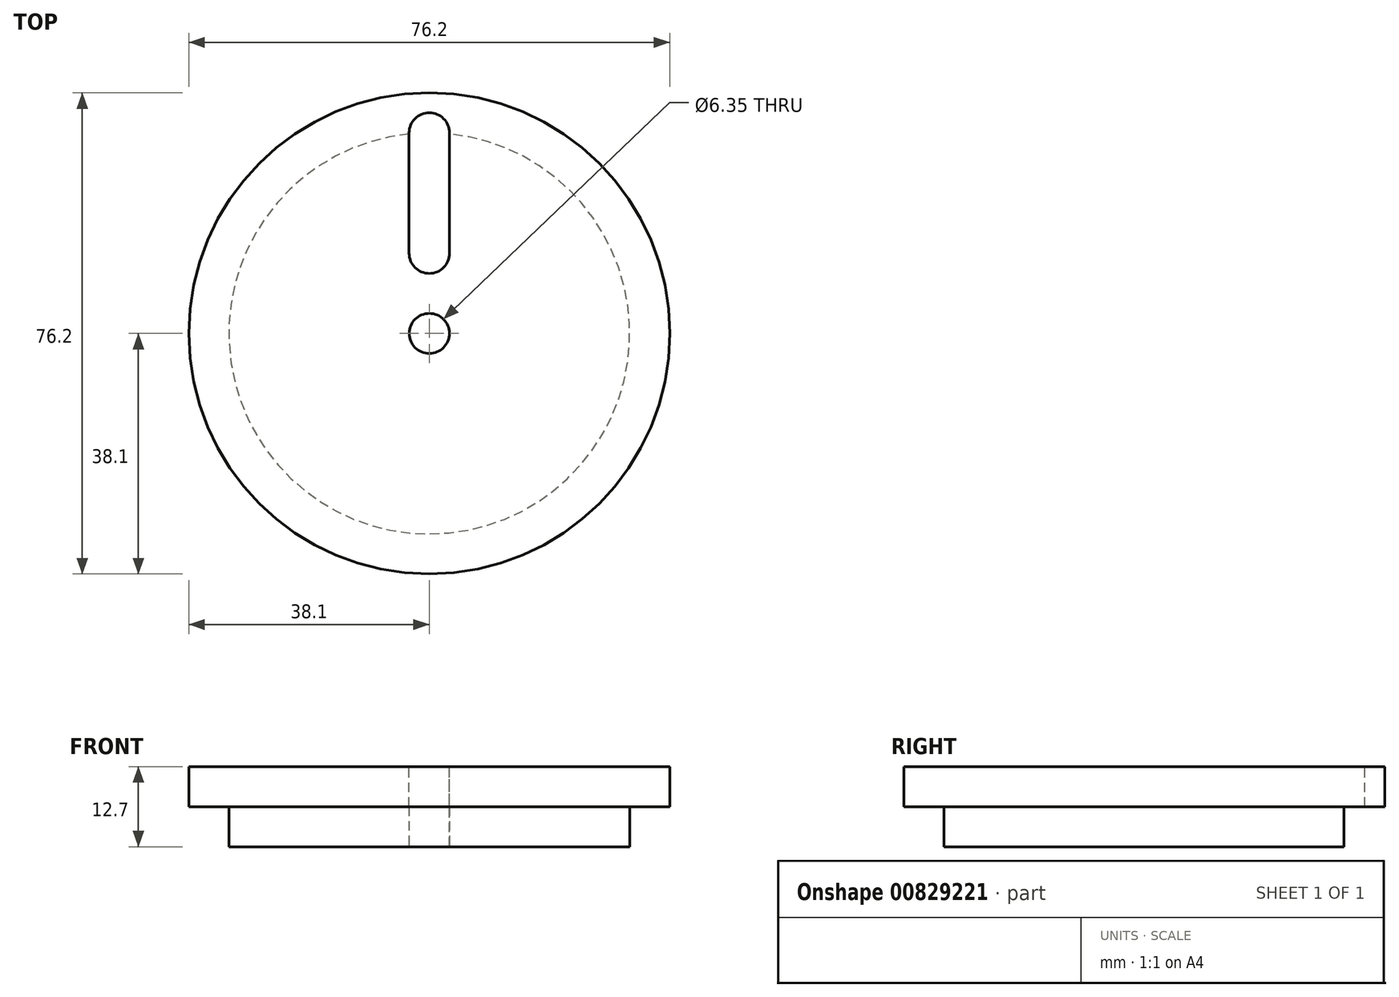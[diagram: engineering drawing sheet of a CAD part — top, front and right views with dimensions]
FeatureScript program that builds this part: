
annotation { "Feature Type Name" : "Feature", "Feature Type Description" : "" }
export const myFeature = defineFeature(function(context is Context, id is Id, definition is map)
    precondition{}
    {
        {
            var Q0;
            Q0=qCreatedBy(makeId("Top.planeOp"),FACE);
            var sketch = newSketch(context, id + "F0", { "sketchPlane" : qUnion([Q0])});
            skCircle(sketch, "E0", {"center": v(0, 0) * mm, "radius": 38.1 * mm});
            skSolve(sketch);
        }
        {
            var Q0;
            Q0 = qSketchRegion(id + "F0", true);
            extrude(context, id + "F1", {"entities" : qUnion([Q0]), "depth" : 12.7 * mm, "offsetDistance" : 25.4 * mm});
        }
        {
            var Q0;
            Q0=makeQuery(id+"F1.opExtrude","CAP_FACE",FACE,{"disambiguationData":[OSD([sQuery(id+"F0.wireOp",EDGE,"E0")])],"isStart":true});
            var sketch = newSketch(context, id + "F2", { "sketchPlane" : qUnion([Q0])});
            skCircle(sketch, "E1.0", {"center": v(0, 0) * mm, "radius": 38.1 * mm});
            skCircle(sketch, "E2", {"center": v(0, 0) * mm, "radius": 31.75 * mm});
            skSolve(sketch);
        }
        {
            var Q0;
            Q0 = qSketchRegion(id + "F2", true);
            extrude(context, id + "F3", {"entities" : qUnion([Q0]), "operationType" : NewBodyOperationType.REMOVE, "oppositeDirection" : true, "depth" : 6.35 * mm, "offsetDistance" : 25.4 * mm});
        }
        {
            var Q0;
            Q0=makeQuery(id+"F1.opExtrude","CAP_FACE",FACE,{"disambiguationData":[OSD([sQuery(id+"F0.wireOp",EDGE,"E0")])],"isStart":false});
            var sketch = newSketch(context, id + "F4", { "sketchPlane" : qUnion([Q0])});
            skCircle(sketch, "E3", {"center": v(0, 0) * mm, "radius": 3.18 * mm});
            skSolve(sketch);
        }
        {
            var Q0;
            Q0 = qSketchRegion(id + "F4", true);
            extrude(context, id + "F5", {"entities" : qUnion([Q0]), "operationType" : NewBodyOperationType.REMOVE, "endBound" : BoundingType.THROUGH_ALL, "oppositeDirection" : true, "depth" : 25.4 * mm, "offsetDistance" : 25.4 * mm});
        }
        {
            var Q0;
            Q0=makeQuery(id+"F1.opExtrude","CAP_FACE",FACE,{"disambiguationData":[OSD([sQuery(id+"F0.wireOp",EDGE,"E0")])],"isStart":false});
            var sketch = newSketch(context, id + "F6", { "sketchPlane" : qUnion([Q0])});
            skArc(sketch, "E4", {"start": v(-3.2, 12.7) * mm, "mid": v(0, 9.5) * mm, "end": v(3.2, 12.7) * mm});
            skArc(sketch, "E5", {"start": v(3.2, 31.75) * mm, "mid": v(0, 34.95) * mm, "end": v(-3.2, 31.75) * mm});
            skLineSegment(sketch, "E6", {"start": v(0, 0) * mm, "end": v(0, 38.1) * mm, "construction": true});
            skLineSegment(sketch, "E7", {"start": v(-3.2, 31.75) * mm, "end": v(-3.2, 12.7) * mm});
            skLineSegment(sketch, "E8", {"start": v(3.2, 31.75) * mm, "end": v(3.2, 12.7) * mm});
            skLineSegment(sketch, "E9", {"start": v(0, 31.75) * mm, "end": v(0, 12.7) * mm, "construction": true});
            skSolve(sketch);
        }
        {
            var Q0;
            Q0 = qSketchRegion(id + "F6", true);
            extrude(context, id + "F7", {"entities" : qUnion([Q0]), "operationType" : NewBodyOperationType.REMOVE, "endBound" : BoundingType.THROUGH_ALL, "oppositeDirection" : true, "depth" : 25.4 * mm, "offsetDistance" : 25.4 * mm});
        }
    });
